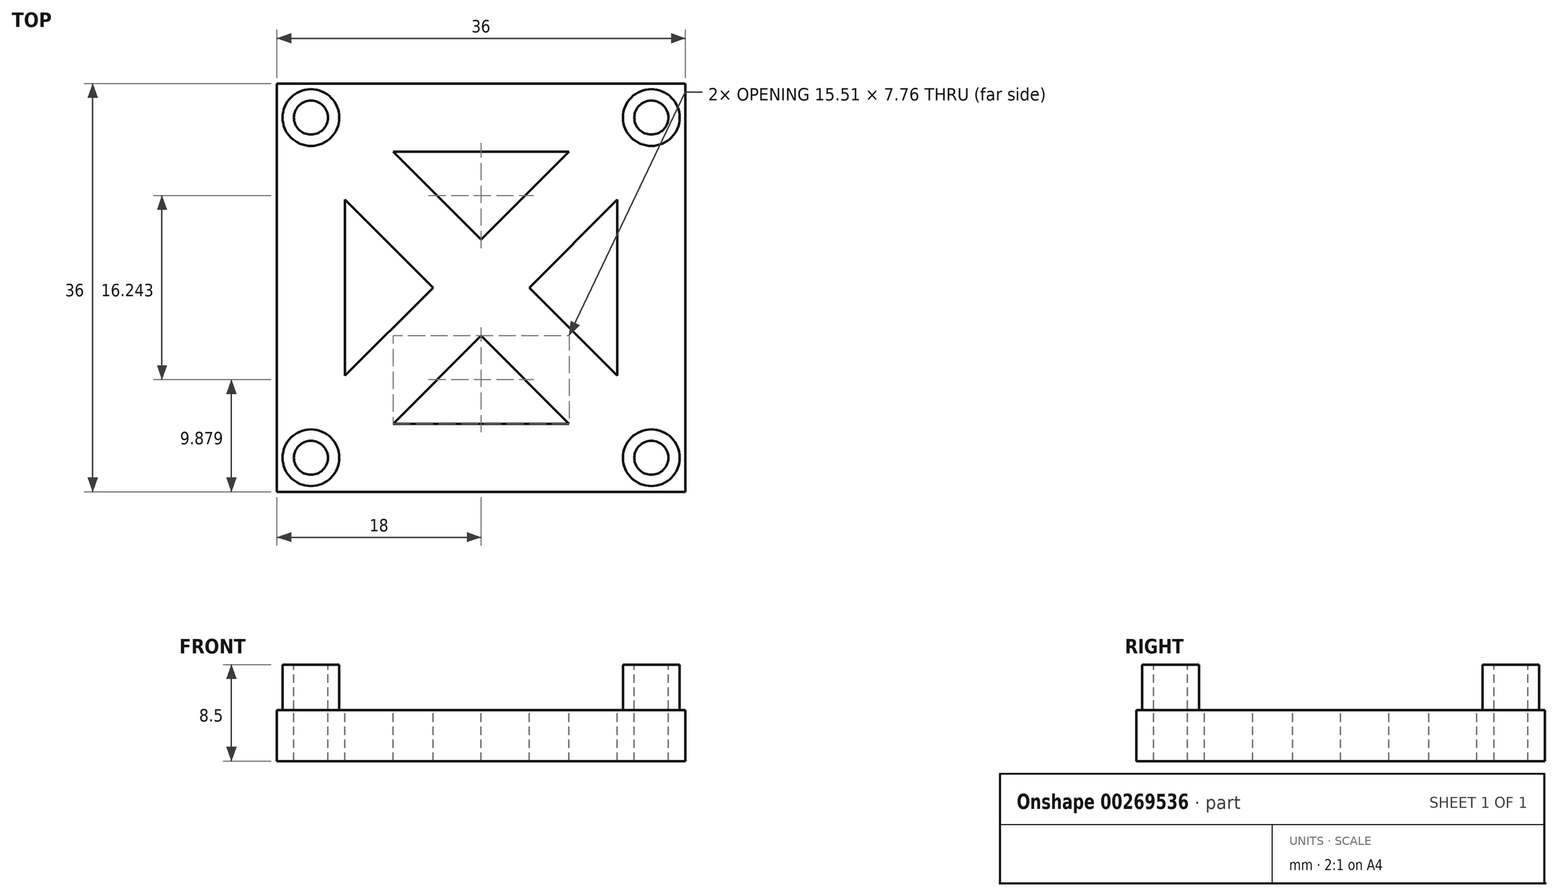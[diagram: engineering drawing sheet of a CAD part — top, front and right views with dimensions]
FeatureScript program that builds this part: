
annotation { "Feature Type Name" : "Feature", "Feature Type Description" : "" }
export const myFeature = defineFeature(function(context is Context, id is Id, definition is map)
    precondition{}
    {
        {
            assignVariable(context, id + "F0", {"name" : "BoardHeight", "anyValue" : 4});
        }
        {
            var Q0;
            Q0=qCreatedBy(makeId("Top.planeOp"),FACE);
            var sketch = newSketch(context, id + "F1", { "sketchPlane" : qUnion([Q0])});
            skLineSegment(sketch, "E0.bottom", {"start": v(15, 15) * mm, "end": v(-15, 15) * mm});
            skLineSegment(sketch, "E0.top", {"start": v(15, -15) * mm, "end": v(-15, -15) * mm});
            skLineSegment(sketch, "E0.left", {"start": v(15, 15) * mm, "end": v(15, -15) * mm});
            skLineSegment(sketch, "E0.right", {"start": v(-15, 15) * mm, "end": v(-15, -15) * mm});
            skPoint(sketch, "E0.middle", {"position": v(0, 0) * mm});
            skCircle(sketch, "E1", {"center": v(-15, 15) * mm, "radius": 1.5 * mm});
            skCircle(sketch, "E2", {"center": v(15, 15) * mm, "radius": 1.5 * mm});
            skCircle(sketch, "E3", {"center": v(15, -15) * mm, "radius": 1.5 * mm});
            skCircle(sketch, "E4", {"center": v(-15, -15) * mm, "radius": 1.5 * mm});
            skCircle(sketch, "E5", {"center": v(-15, 15) * mm, "radius": 2.5 * mm});
            skCircle(sketch, "E6", {"center": v(15, 15) * mm, "radius": 2.5 * mm});
            skCircle(sketch, "E7", {"center": v(15, -15) * mm, "radius": 2.5 * mm});
            skCircle(sketch, "E8", {"center": v(-15, -15) * mm, "radius": 2.5 * mm});
            skLineSegment(sketch, "E9.0", {"start": v(-18, 18) * mm, "end": v(-18, -18) * mm});
            skLineSegment(sketch, "E9.1", {"start": v(18, 18) * mm, "end": v(-18, 18) * mm});
            skLineSegment(sketch, "E9.2", {"start": v(18, 18) * mm, "end": v(18, -18) * mm});
            skLineSegment(sketch, "E9.3", {"start": v(18, -18) * mm, "end": v(-18, -18) * mm});
            skLineSegment(sketch, "E10.0", {"start": v(-12, 12) * mm, "end": v(-12, -12) * mm});
            skLineSegment(sketch, "E10.1", {"start": v(12, 12) * mm, "end": v(-12, 12) * mm});
            skLineSegment(sketch, "E10.2", {"start": v(12, 12) * mm, "end": v(12, -12) * mm});
            skLineSegment(sketch, "E10.3", {"start": v(12, -12) * mm, "end": v(-12, -12) * mm});
            skLineSegment(sketch, "E11", {"start": v(-15, -15) * mm, "end": v(0, 0) * mm});
            skLineSegment(sketch, "E12", {"start": v(0, 0) * mm, "end": v(15, -15) * mm});
            skLineSegment(sketch, "E13", {"start": v(0, 0) * mm, "end": v(15, 15) * mm});
            skLineSegment(sketch, "E14", {"start": v(0, 0) * mm, "end": v(-15, 15) * mm});
            skLineSegment(sketch, "E15", {"start": v(2.12, 2.12) * mm, "end": v(-7.76, 12) * mm});
            skLineSegment(sketch, "E16", {"start": v(-2.12, -2.12) * mm, "end": v(-12, 7.76) * mm});
            skLineSegment(sketch, "E17", {"start": v(2.12, 2.12) * mm, "end": v(12, -7.76) * mm});
            skLineSegment(sketch, "E18", {"start": v(-2.12, -2.12) * mm, "end": v(7.76, -12) * mm});
            skLineSegment(sketch, "E19", {"start": v(-4.24, 0) * mm, "end": v(-12, -7.76) * mm});
            skLineSegment(sketch, "E20", {"start": v(0, -4.24) * mm, "end": v(-7.76, -12) * mm});
            skLineSegment(sketch, "E21", {"start": v(4.24, 0) * mm, "end": v(12, 7.76) * mm});
            skLineSegment(sketch, "E22", {"start": v(0, 4.24) * mm, "end": v(7.76, 12) * mm});
            skSolve(sketch);
        }
        {
            var Q0;
            {var subQ4=sQuery(id+"F1.wireOp",EDGE,"E5");var subQ5=sQuery(id+"F1.wireOp",EDGE,"E0.right");var subQ6=makeQuery(id+"F1.imprint","INTERSECT",VERTEX,{"derivedFrom":[subQ5,subQ4]});Q0=makeQuery(id+"F1.imprint","IMPRINT",FACE,{"disambiguationData":[TD([[makeQuery(id+"F1.imprint","IMPRINT",EDGE,{"disambiguationData":[TD([[subQ6,-1.0]])],"derivedFrom":subQ5}),1.0]])]});}
            var Q1;
            Q1=makeQuery(id+"F1.imprint","IMPRINT",FACE,{"disambiguationData":[TD([[makeQuery(id+"F1.imprint","IMPRINT",EDGE,{"derivedFrom":sQuery(id+"F1.wireOp",EDGE,"E9.0")}),1.0]])]});
            var Q2;
            {var subQ0=sQuery(id+"F1.wireOp",EDGE,"E16");var subQ5=sQuery(id+"F1.wireOp",EDGE,"E10.0");var subQ8=makeQuery(id+"F1.imprint","INTERSECT",VERTEX,{"derivedFrom":[subQ5,subQ0]});Q2=makeQuery(id+"F1.imprint","IMPRINT",FACE,{"disambiguationData":[TD([[makeQuery(id+"F1.imprint","IMPRINT",EDGE,{"disambiguationData":[TD([[subQ8,1.0]])],"derivedFrom":subQ0}),-1.0]])]});}
            var Q3;
            {var subQ1=sQuery(id+"F1.wireOp",EDGE,"E10.1");var subQ5=sQuery(id+"F1.wireOp",EDGE,"E15");var subQ8=makeQuery(id+"F1.imprint","INTERSECT",VERTEX,{"derivedFrom":[subQ1,subQ5]});Q3=makeQuery(id+"F1.imprint","IMPRINT",FACE,{"disambiguationData":[TD([[makeQuery(id+"F1.imprint","IMPRINT",EDGE,{"disambiguationData":[TD([[subQ8,1.0]])],"derivedFrom":subQ5}),1.0]])]});}
            var Q4;
            {var subQ4=sQuery(id+"F1.wireOp",EDGE,"E6");var subQ5=sQuery(id+"F1.wireOp",EDGE,"E0.bottom");var subQ6=makeQuery(id+"F1.imprint","INTERSECT",VERTEX,{"derivedFrom":[subQ5,subQ4]});Q4=makeQuery(id+"F1.imprint","IMPRINT",FACE,{"disambiguationData":[TD([[makeQuery(id+"F1.imprint","IMPRINT",EDGE,{"disambiguationData":[TD([[subQ6,-1.0]])],"derivedFrom":subQ5}),1.0]])]});}
            var Q5;
            {var subQ0=sQuery(id+"F1.wireOp",EDGE,"E5");var subQ1=sQuery(id+"F1.wireOp",EDGE,"E0.bottom");var subQ2=makeQuery(id+"F1.imprint","INTERSECT",VERTEX,{"derivedFrom":[subQ1,subQ0]});Q5=makeQuery(id+"F1.imprint","IMPRINT",FACE,{"disambiguationData":[TD([[makeQuery(id+"F1.imprint","IMPRINT",EDGE,{"disambiguationData":[TD([[subQ2,-1.0]])],"derivedFrom":subQ1}),-1.0]])]});}
            var Q6;
            {var subQ0=sQuery(id+"F1.wireOp",EDGE,"E1");var subQ1=sQuery(id+"F1.wireOp",EDGE,"E0.right");var subQ2=makeQuery(id+"F1.imprint","INTERSECT",VERTEX,{"derivedFrom":[subQ1,subQ0]});Q6=makeQuery(id+"F1.imprint","IMPRINT",FACE,{"disambiguationData":[TD([[makeQuery(id+"F1.imprint","IMPRINT",EDGE,{"disambiguationData":[TD([[subQ2,-1.0]])],"derivedFrom":subQ1}),1.0]])]});}
            var Q7;
            {var subQ0=sQuery(id+"F1.wireOp",EDGE,"E5");var subQ1=sQuery(id+"F1.wireOp",EDGE,"E0.bottom");var subQ2=makeQuery(id+"F1.imprint","INTERSECT",VERTEX,{"derivedFrom":[subQ1,subQ0]});Q7=makeQuery(id+"F1.imprint","IMPRINT",FACE,{"disambiguationData":[TD([[makeQuery(id+"F1.imprint","IMPRINT",EDGE,{"disambiguationData":[TD([[subQ2,-1.0]])],"derivedFrom":subQ1}),1.0]])]});}
            var Q8;
            {var subQ1=sQuery(id+"F1.wireOp",EDGE,"E0.top");var subQ5=sQuery(id+"F1.wireOp",EDGE,"E7");var subQ6=makeQuery(id+"F1.imprint","INTERSECT",VERTEX,{"derivedFrom":[subQ1,subQ5]});Q8=makeQuery(id+"F1.imprint","IMPRINT",FACE,{"disambiguationData":[TD([[makeQuery(id+"F1.imprint","IMPRINT",EDGE,{"disambiguationData":[TD([[subQ6,-1.0]])],"derivedFrom":subQ1}),-1.0]])]});}
            var Q9;
            {var subQ5=sQuery(id+"F1.wireOp",EDGE,"E0.left");var subQ9=sQuery(id+"F1.wireOp",EDGE,"E6");var subQ11=makeQuery(id+"F1.imprint","INTERSECT",VERTEX,{"derivedFrom":[subQ5,subQ9]});Q9=makeQuery(id+"F1.imprint","IMPRINT",FACE,{"disambiguationData":[TD([[makeQuery(id+"F1.imprint","IMPRINT",EDGE,{"disambiguationData":[TD([[subQ11,-1.0]])],"derivedFrom":subQ5}),-1.0]])]});}
            var Q10;
            {var subQ0=sQuery(id+"F1.wireOp",EDGE,"E17");var subQ6=sQuery(id+"F1.wireOp",EDGE,"E10.2");var subQ8=makeQuery(id+"F1.imprint","INTERSECT",VERTEX,{"derivedFrom":[subQ6,subQ0]});Q10=makeQuery(id+"F1.imprint","IMPRINT",FACE,{"disambiguationData":[TD([[makeQuery(id+"F1.imprint","IMPRINT",EDGE,{"disambiguationData":[TD([[subQ8,1.0]])],"derivedFrom":subQ0}),-1.0]])]});}
            var Q11;
            {var subQ1=sQuery(id+"F1.wireOp",EDGE,"E10.3");var subQ5=sQuery(id+"F1.wireOp",EDGE,"E18");var subQ8=makeQuery(id+"F1.imprint","INTERSECT",VERTEX,{"derivedFrom":[subQ1,subQ5]});Q11=makeQuery(id+"F1.imprint","IMPRINT",FACE,{"disambiguationData":[TD([[makeQuery(id+"F1.imprint","IMPRINT",EDGE,{"disambiguationData":[TD([[subQ8,1.0]])],"derivedFrom":subQ5}),1.0]])]});}
            var Q12;
            {var subQ3=sQuery(id+"F1.wireOp",EDGE,"E20");Q12=makeQuery(id+"F1.imprint","IMPRINT",FACE,{"disambiguationData":[TD([[makeQuery(id+"F1.imprint","IMPRINT",EDGE,{"derivedFrom":subQ3}),-1.0]])]});}
            var Q13;
            {var subQ3=sQuery(id+"F1.wireOp",EDGE,"E19");Q13=makeQuery(id+"F1.imprint","IMPRINT",FACE,{"disambiguationData":[TD([[makeQuery(id+"F1.imprint","IMPRINT",EDGE,{"derivedFrom":subQ3}),1.0]])]});}
            var Q14;
            {var subQ3=sQuery(id+"F1.wireOp",EDGE,"E22");Q14=makeQuery(id+"F1.imprint","IMPRINT",FACE,{"disambiguationData":[TD([[makeQuery(id+"F1.imprint","IMPRINT",EDGE,{"derivedFrom":subQ3}),-1.0]])]});}
            var Q15;
            {var subQ3=sQuery(id+"F1.wireOp",EDGE,"E21");Q15=makeQuery(id+"F1.imprint","IMPRINT",FACE,{"disambiguationData":[TD([[makeQuery(id+"F1.imprint","IMPRINT",EDGE,{"derivedFrom":subQ3}),1.0]])]});}
            var Q16;
            {var subQ0=sQuery(id+"F1.wireOp",EDGE,"E2");var subQ1=sQuery(id+"F1.wireOp",EDGE,"E0.bottom");var subQ2=makeQuery(id+"F1.imprint","INTERSECT",VERTEX,{"derivedFrom":[subQ1,subQ0]});Q16=makeQuery(id+"F1.imprint","IMPRINT",FACE,{"disambiguationData":[TD([[makeQuery(id+"F1.imprint","IMPRINT",EDGE,{"disambiguationData":[TD([[subQ2,-1.0]])],"derivedFrom":subQ1}),-1.0]])]});}
            var Q17;
            {var subQ0=sQuery(id+"F1.wireOp",EDGE,"E2");var subQ1=sQuery(id+"F1.wireOp",EDGE,"E0.left");var subQ2=makeQuery(id+"F1.imprint","INTERSECT",VERTEX,{"derivedFrom":[subQ1,subQ0]});Q17=makeQuery(id+"F1.imprint","IMPRINT",FACE,{"disambiguationData":[TD([[makeQuery(id+"F1.imprint","IMPRINT",EDGE,{"disambiguationData":[TD([[subQ2,-1.0]])],"derivedFrom":subQ1}),-1.0]])]});}
            var Q18;
            {var subQ0=sQuery(id+"F1.wireOp",EDGE,"E2");var subQ1=sQuery(id+"F1.wireOp",EDGE,"E0.bottom");var subQ2=makeQuery(id+"F1.imprint","INTERSECT",VERTEX,{"derivedFrom":[subQ1,subQ0]});Q18=makeQuery(id+"F1.imprint","IMPRINT",FACE,{"disambiguationData":[TD([[makeQuery(id+"F1.imprint","IMPRINT",EDGE,{"disambiguationData":[TD([[subQ2,-1.0]])],"derivedFrom":subQ1}),1.0]])]});}
            var Q19;
            {var subQ0=sQuery(id+"F1.wireOp",EDGE,"E3");var subQ1=sQuery(id+"F1.wireOp",EDGE,"E0.top");var subQ2=makeQuery(id+"F1.imprint","INTERSECT",VERTEX,{"derivedFrom":[subQ1,subQ0]});Q19=makeQuery(id+"F1.imprint","IMPRINT",FACE,{"disambiguationData":[TD([[makeQuery(id+"F1.imprint","IMPRINT",EDGE,{"disambiguationData":[TD([[subQ2,-1.0]])],"derivedFrom":subQ1}),1.0]])]});}
            var Q20;
            {var subQ0=sQuery(id+"F1.wireOp",EDGE,"E3");var subQ1=sQuery(id+"F1.wireOp",EDGE,"E0.top");var subQ2=makeQuery(id+"F1.imprint","INTERSECT",VERTEX,{"derivedFrom":[subQ1,subQ0]});Q20=makeQuery(id+"F1.imprint","IMPRINT",FACE,{"disambiguationData":[TD([[makeQuery(id+"F1.imprint","IMPRINT",EDGE,{"disambiguationData":[TD([[subQ2,-1.0]])],"derivedFrom":subQ1}),-1.0]])]});}
            var Q21;
            {var subQ0=sQuery(id+"F1.wireOp",EDGE,"E7");var subQ1=sQuery(id+"F1.wireOp",EDGE,"E0.left");var subQ2=makeQuery(id+"F1.imprint","INTERSECT",VERTEX,{"derivedFrom":[subQ1,subQ0]});Q21=makeQuery(id+"F1.imprint","IMPRINT",FACE,{"disambiguationData":[TD([[makeQuery(id+"F1.imprint","IMPRINT",EDGE,{"disambiguationData":[TD([[subQ2,-1.0]])],"derivedFrom":subQ1}),-1.0]])]});}
            var Q22;
            {var subQ0=sQuery(id+"F1.wireOp",EDGE,"E8");var subQ1=sQuery(id+"F1.wireOp",EDGE,"E0.top");var subQ2=makeQuery(id+"F1.imprint","INTERSECT",VERTEX,{"derivedFrom":[subQ1,subQ0]});Q22=makeQuery(id+"F1.imprint","IMPRINT",FACE,{"disambiguationData":[TD([[makeQuery(id+"F1.imprint","IMPRINT",EDGE,{"disambiguationData":[TD([[subQ2,-1.0]])],"derivedFrom":subQ1}),1.0]])]});}
            var Q23;
            {var subQ0=sQuery(id+"F1.wireOp",EDGE,"E8");var subQ1=sQuery(id+"F1.wireOp",EDGE,"E0.top");var subQ2=makeQuery(id+"F1.imprint","INTERSECT",VERTEX,{"derivedFrom":[subQ1,subQ0]});Q23=makeQuery(id+"F1.imprint","IMPRINT",FACE,{"disambiguationData":[TD([[makeQuery(id+"F1.imprint","IMPRINT",EDGE,{"disambiguationData":[TD([[subQ2,-1.0]])],"derivedFrom":subQ1}),-1.0]])]});}
            var Q24;
            {var subQ0=sQuery(id+"F1.wireOp",EDGE,"E8");var subQ1=sQuery(id+"F1.wireOp",EDGE,"E0.right");var subQ2=makeQuery(id+"F1.imprint","INTERSECT",VERTEX,{"derivedFrom":[subQ1,subQ0]});Q24=makeQuery(id+"F1.imprint","IMPRINT",FACE,{"disambiguationData":[TD([[makeQuery(id+"F1.imprint","IMPRINT",EDGE,{"disambiguationData":[TD([[subQ2,-1.0]])],"derivedFrom":subQ1}),1.0]])]});}
            extrude(context, id + "F2", {"entities" : qUnion([Q0, Q1, Q2, Q3, Q4, Q5, Q6, Q7, Q8, Q9, Q10, Q11, Q12, Q13, Q14, Q15, Q16, Q17, Q18, Q19, Q20, Q21, Q22, Q23, Q24]), "oppositeDirection" : true, "depth" : 4.5 * mm});
        }
        {
            var Q0;
            {var subQ0=sQuery(id+"F1.wireOp",EDGE,"E5");var subQ1=sQuery(id+"F1.wireOp",EDGE,"E0.bottom");var subQ2=makeQuery(id+"F1.imprint","INTERSECT",VERTEX,{"derivedFrom":[subQ1,subQ0]});Q0=makeQuery(id+"F1.imprint","IMPRINT",FACE,{"disambiguationData":[TD([[makeQuery(id+"F1.imprint","IMPRINT",EDGE,{"disambiguationData":[TD([[subQ2,-1.0]])],"derivedFrom":subQ1}),-1.0]])]});}
            var Q1;
            {var subQ0=sQuery(id+"F1.wireOp",EDGE,"E1");var subQ1=sQuery(id+"F1.wireOp",EDGE,"E0.right");var subQ2=makeQuery(id+"F1.imprint","INTERSECT",VERTEX,{"derivedFrom":[subQ1,subQ0]});Q1=makeQuery(id+"F1.imprint","IMPRINT",FACE,{"disambiguationData":[TD([[makeQuery(id+"F1.imprint","IMPRINT",EDGE,{"disambiguationData":[TD([[subQ2,-1.0]])],"derivedFrom":subQ1}),1.0]])]});}
            var Q2;
            {var subQ0=sQuery(id+"F1.wireOp",EDGE,"E5");var subQ1=sQuery(id+"F1.wireOp",EDGE,"E0.bottom");var subQ2=makeQuery(id+"F1.imprint","INTERSECT",VERTEX,{"derivedFrom":[subQ1,subQ0]});Q2=makeQuery(id+"F1.imprint","IMPRINT",FACE,{"disambiguationData":[TD([[makeQuery(id+"F1.imprint","IMPRINT",EDGE,{"disambiguationData":[TD([[subQ2,-1.0]])],"derivedFrom":subQ1}),1.0]])]});}
            var Q3;
            {var subQ0=sQuery(id+"F1.wireOp",EDGE,"E2");var subQ1=sQuery(id+"F1.wireOp",EDGE,"E0.bottom");var subQ2=makeQuery(id+"F1.imprint","INTERSECT",VERTEX,{"derivedFrom":[subQ1,subQ0]});Q3=makeQuery(id+"F1.imprint","IMPRINT",FACE,{"disambiguationData":[TD([[makeQuery(id+"F1.imprint","IMPRINT",EDGE,{"disambiguationData":[TD([[subQ2,-1.0]])],"derivedFrom":subQ1}),-1.0]])]});}
            var Q4;
            {var subQ0=sQuery(id+"F1.wireOp",EDGE,"E2");var subQ1=sQuery(id+"F1.wireOp",EDGE,"E0.left");var subQ2=makeQuery(id+"F1.imprint","INTERSECT",VERTEX,{"derivedFrom":[subQ1,subQ0]});Q4=makeQuery(id+"F1.imprint","IMPRINT",FACE,{"disambiguationData":[TD([[makeQuery(id+"F1.imprint","IMPRINT",EDGE,{"disambiguationData":[TD([[subQ2,-1.0]])],"derivedFrom":subQ1}),-1.0]])]});}
            var Q5;
            {var subQ0=sQuery(id+"F1.wireOp",EDGE,"E2");var subQ1=sQuery(id+"F1.wireOp",EDGE,"E0.bottom");var subQ2=makeQuery(id+"F1.imprint","INTERSECT",VERTEX,{"derivedFrom":[subQ1,subQ0]});Q5=makeQuery(id+"F1.imprint","IMPRINT",FACE,{"disambiguationData":[TD([[makeQuery(id+"F1.imprint","IMPRINT",EDGE,{"disambiguationData":[TD([[subQ2,-1.0]])],"derivedFrom":subQ1}),1.0]])]});}
            var Q6;
            {var subQ0=sQuery(id+"F1.wireOp",EDGE,"E8");var subQ1=sQuery(id+"F1.wireOp",EDGE,"E0.top");var subQ2=makeQuery(id+"F1.imprint","INTERSECT",VERTEX,{"derivedFrom":[subQ1,subQ0]});Q6=makeQuery(id+"F1.imprint","IMPRINT",FACE,{"disambiguationData":[TD([[makeQuery(id+"F1.imprint","IMPRINT",EDGE,{"disambiguationData":[TD([[subQ2,-1.0]])],"derivedFrom":subQ1}),1.0]])]});}
            var Q7;
            {var subQ0=sQuery(id+"F1.wireOp",EDGE,"E8");var subQ1=sQuery(id+"F1.wireOp",EDGE,"E0.right");var subQ2=makeQuery(id+"F1.imprint","INTERSECT",VERTEX,{"derivedFrom":[subQ1,subQ0]});Q7=makeQuery(id+"F1.imprint","IMPRINT",FACE,{"disambiguationData":[TD([[makeQuery(id+"F1.imprint","IMPRINT",EDGE,{"disambiguationData":[TD([[subQ2,-1.0]])],"derivedFrom":subQ1}),1.0]])]});}
            var Q8;
            {var subQ0=sQuery(id+"F1.wireOp",EDGE,"E8");var subQ1=sQuery(id+"F1.wireOp",EDGE,"E0.top");var subQ2=makeQuery(id+"F1.imprint","INTERSECT",VERTEX,{"derivedFrom":[subQ1,subQ0]});Q8=makeQuery(id+"F1.imprint","IMPRINT",FACE,{"disambiguationData":[TD([[makeQuery(id+"F1.imprint","IMPRINT",EDGE,{"disambiguationData":[TD([[subQ2,-1.0]])],"derivedFrom":subQ1}),-1.0]])]});}
            var Q9;
            {var subQ0=sQuery(id+"F1.wireOp",EDGE,"E7");var subQ1=sQuery(id+"F1.wireOp",EDGE,"E0.left");var subQ2=makeQuery(id+"F1.imprint","INTERSECT",VERTEX,{"derivedFrom":[subQ1,subQ0]});Q9=makeQuery(id+"F1.imprint","IMPRINT",FACE,{"disambiguationData":[TD([[makeQuery(id+"F1.imprint","IMPRINT",EDGE,{"disambiguationData":[TD([[subQ2,-1.0]])],"derivedFrom":subQ1}),-1.0]])]});}
            var Q10;
            {var subQ0=sQuery(id+"F1.wireOp",EDGE,"E3");var subQ1=sQuery(id+"F1.wireOp",EDGE,"E0.top");var subQ2=makeQuery(id+"F1.imprint","INTERSECT",VERTEX,{"derivedFrom":[subQ1,subQ0]});Q10=makeQuery(id+"F1.imprint","IMPRINT",FACE,{"disambiguationData":[TD([[makeQuery(id+"F1.imprint","IMPRINT",EDGE,{"disambiguationData":[TD([[subQ2,-1.0]])],"derivedFrom":subQ1}),-1.0]])]});}
            var Q11;
            {var subQ0=sQuery(id+"F1.wireOp",EDGE,"E3");var subQ1=sQuery(id+"F1.wireOp",EDGE,"E0.top");var subQ2=makeQuery(id+"F1.imprint","INTERSECT",VERTEX,{"derivedFrom":[subQ1,subQ0]});Q11=makeQuery(id+"F1.imprint","IMPRINT",FACE,{"disambiguationData":[TD([[makeQuery(id+"F1.imprint","IMPRINT",EDGE,{"disambiguationData":[TD([[subQ2,-1.0]])],"derivedFrom":subQ1}),1.0]])]});}
            extrude(context, id + "F3", {"entities" : qUnion([Q0, Q1, Q2, Q3, Q4, Q5, Q6, Q7, Q8, Q9, Q10, Q11]), "operationType" : NewBodyOperationType.ADD, "depth" : (getVariable(context, 'BoardHeight')) * mm});
        }
    });
